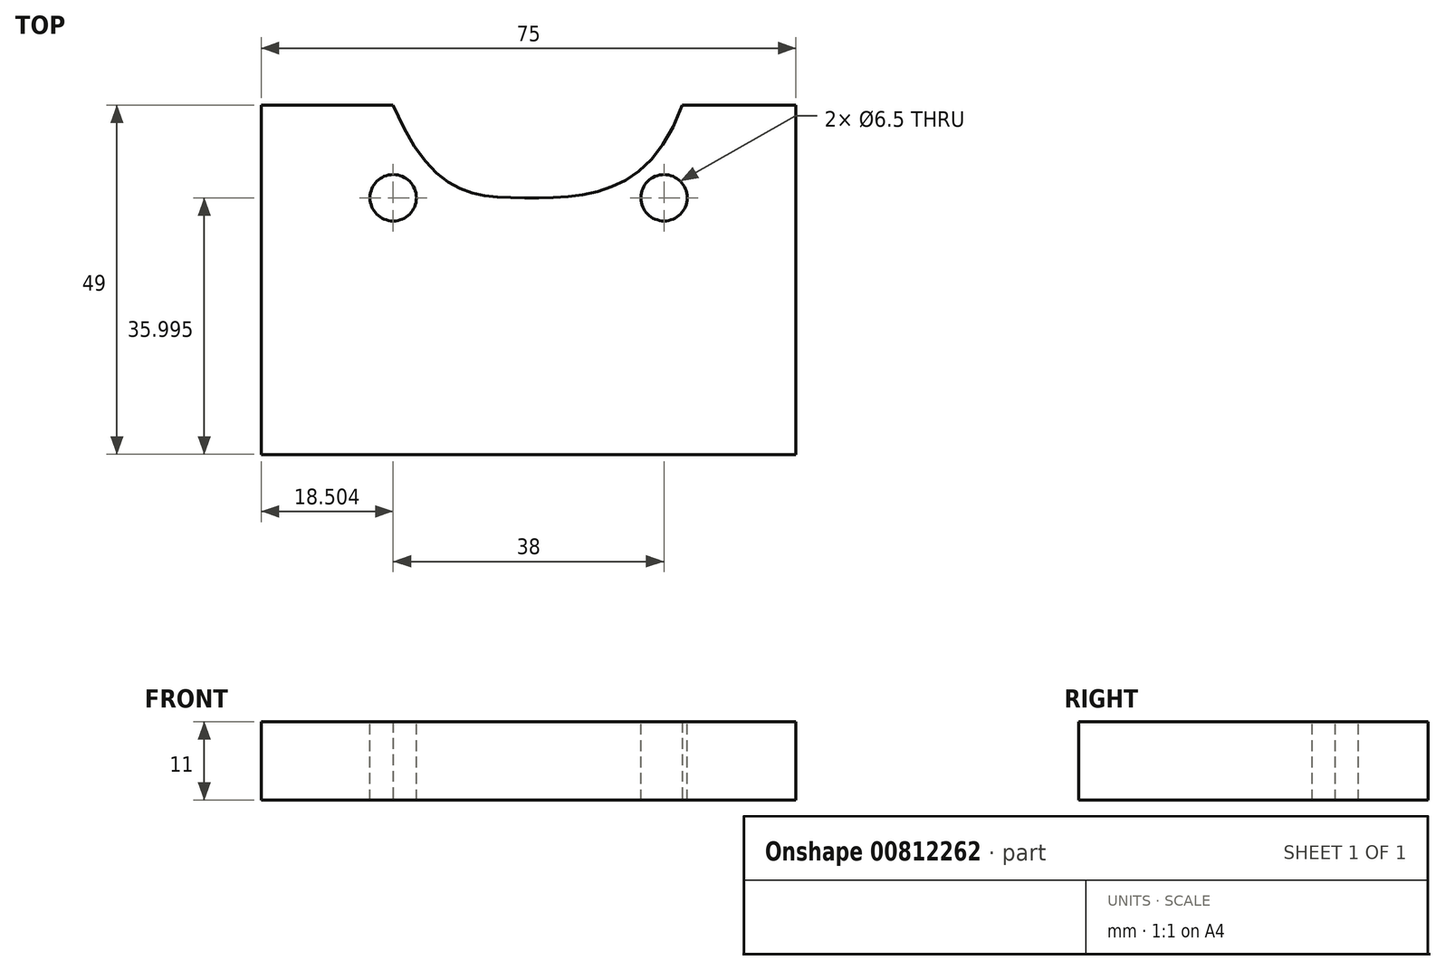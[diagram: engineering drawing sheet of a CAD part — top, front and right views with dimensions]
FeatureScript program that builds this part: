
annotation { "Feature Type Name" : "Feature", "Feature Type Description" : "" }
export const myFeature = defineFeature(function(context is Context, id is Id, definition is map)
    precondition{}
    {
        {
            var Q0;
            Q0=qCreatedBy(makeId("Top.planeOp"),FACE);
            var sketch = newSketch(context, id + "F0", { "sketchPlane" : qUnion([Q0])});
            skLineSegment(sketch, "E0", {"start": v(-37.35, -25.7) * mm, "end": v(37.65, -25.7) * mm});
            skLineSegment(sketch, "E1", {"start": v(37.65, 23.3) * mm, "end": v(-37.35, 23.3) * mm});
            skLineSegment(sketch, "E2", {"start": v(-37.35, 23.3) * mm, "end": v(-37.35, -25.7) * mm});
            skLineSegment(sketch, "E3", {"start": v(37.65, -25.7) * mm, "end": v(37.65, 23.3) * mm});
            skPoint(sketch, "E4", {"position": v(19.15, 10.3) * mm});
            skPoint(sketch, "E5", {"position": v(-18.85, 10.3) * mm});
            skFitSpline(sketch, "E6", {"points": [v(-18.85, 23.3) * mm, v(0, 10.3) * mm, v(21.69, 23.3) * mm], "startDerivative": vector(33.62, -79.99) * mm, "endDerivative": vector(27.02, 76.11) * mm});
            skSolve(sketch);
        }
        {
            var Q0;
            Q0 = qSketchRegion(id + "F0", true);
            extrude(context, id + "F1", {"entities" : qUnion([Q0]), "depth" : 11 * mm, "offsetDistance" : 25 * mm});
        }
        {
            var Q0;
            Q0=sQuery(id+"F0.wireOp",VERTEX,"E4");
            var Q1;
            Q1=sQuery(id+"F0.wireOp",VERTEX,"E5");
            var Q2;
            Q2=makeQuery(id+"F1.opExtrude","SWEPT_BODY",BODY,{"disambiguationData":[OSD([sQuery(id+"F0.wireOp",EDGE,"E0"),sQuery(id+"F0.wireOp",EDGE,"E1"),sQuery(id+"F0.wireOp",EDGE,"E2"),sQuery(id+"F0.wireOp",EDGE,"E3")])]});
            hole(context, id + "F2", {"style" : HoleStyle.SIMPLE, "endStyle" : HoleEndStyle.THROUGH, "oppositeDirection" : true, "holeDiameter" : 6.5 * mm, "majorDiameter" : 5 * mm, "isTappedThrough" : true, "tappedDepth" : 12 * mm, "tapClearance" : 3, "locations" : qUnion([Q0, Q1]), "scope" : qUnion([Q2])});
        }
        {
            var Q0;
            {var subQ0=sQuery(id+"F0.wireOp",EDGE,"E6");Q0=makeQuery(id+"F0.imprint","IMPRINT",FACE,{"disambiguationData":[TD([[makeQuery(id+"F0.imprint","IMPRINT",EDGE,{"derivedFrom":subQ0}),1.0]])]});}
            extrude(context, id + "F3", {"entities" : qUnion([Q0]), "operationType" : NewBodyOperationType.REMOVE, "depth" : 38.9 * mm, "offsetDistance" : 25 * mm});
        }
    });
